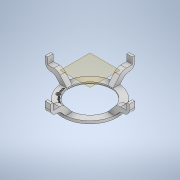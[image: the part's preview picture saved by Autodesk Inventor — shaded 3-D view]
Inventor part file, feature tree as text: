
AUTODESK INVENTOR PART (.ipt)
format: ipt  version: 2022 (Build 260153000, 153)  size: 623,616 bytes
history: native  units: in
note: dims shown in document units (in); Inventor stores cm internally (conversion verified against a paired STEP export)
features: extrude x4, sketch x4, plane x3, emboss x1, pattern_circular x1
ambient origin geometry x8: Origin, YZ Plane, XZ Plane, XY Plane, X Axis, Y Axis, Z Axis, Center Point
bodies: Solid1 (feature_tree)
feature tree (13):
  extrude  "Extrusion1"  Depth=0.3937in
  plane  "Work Plane2"
  extrude  "Extrusion3"  Depth=0.1969in
  plane  "Work Plane3"
  emboss  "Emboss1"
  extrude  "Extrusion4"  Depth=0.0787in TaperAngle=0.0deg
  pattern_circular  "Circular Pattern2"  Count=2  [1 undecoded]
  plane  "Work Plane4"
  extrude  "Extrusion5"  Depth=2.8346in
  sketch  "Sketch1"  dims[d0=0.3937in d1=3.1516in]
  sketch  "Sketch4"  dims[d2=0.1969in d3=0.0in d10=2.9528in]
  sketch  "Sketch6"  dims[d11=3.1575in d12=0.0787in d13=0.0in]
  sketch  "Sketch7"  dims[d17=0.0394in d18=0.0in d27=0.7874in d28=2.8346in d29=0.1969in d31=0.4724in d32=0.7874in d35=0.3937in d36=0.0in d37=0.315in d39=0.5906in d40=0.5906in d41=0.0787in d42=1.5748in d43=360.0deg d45=0.0in d47=0.7874in d48=5.7323in d49=0.0in d50=0.0in d51=0.3937in]
note: 1 required parameter value undecoded (feature->parameter linkage not recoverable at this tier; creation-order binding heuristic only, values carry confidence <= 0.55)
